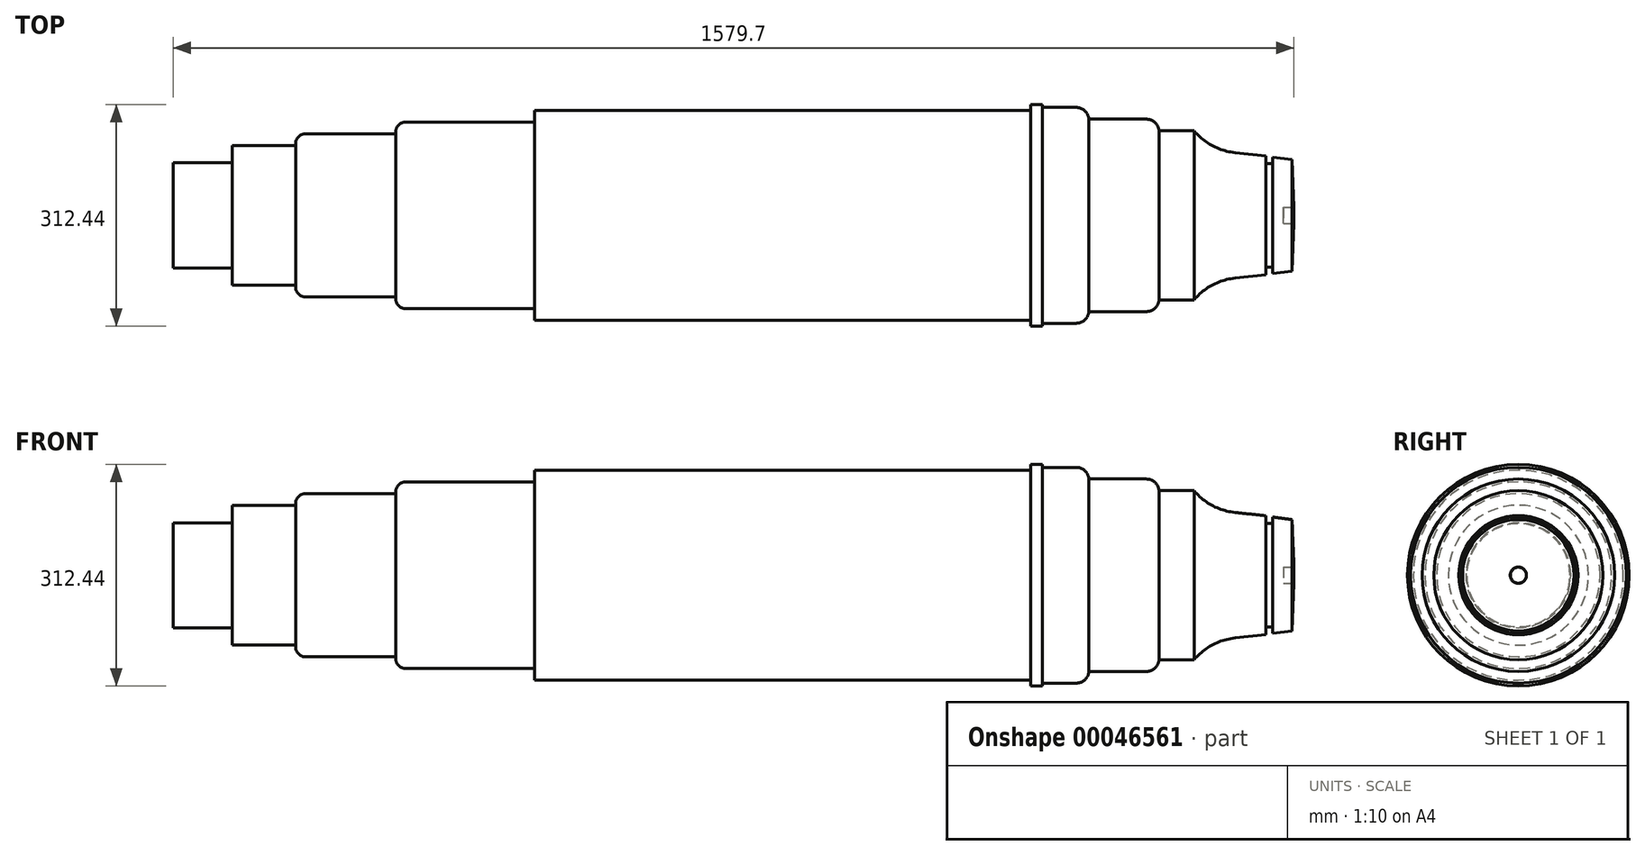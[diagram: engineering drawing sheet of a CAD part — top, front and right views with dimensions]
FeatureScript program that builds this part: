
annotation { "Feature Type Name" : "Feature", "Feature Type Description" : "" }
export const myFeature = defineFeature(function(context is Context, id is Id, definition is map)
    precondition{}
    {
        {
            var Q0;
            Q0=qCreatedBy(makeId("Front.planeOp"),FACE);
            var sketch = newSketch(context, id + "F0", { "sketchPlane" : qUnion([Q0])});
            skLineSegment(sketch, "E0", {"start": v(-826.12, 0) * mm, "end": v(-826.12, 74) * mm});
            skLineSegment(sketch, "E1", {"start": v(-826.12, 74) * mm, "end": v(-742.99, 74) * mm});
            skLineSegment(sketch, "E2", {"start": v(-742.99, 74) * mm, "end": v(-742.99, 98.67) * mm});
            skLineSegment(sketch, "E3", {"start": v(-742.99, 98.67) * mm, "end": v(-653.4, 98.67) * mm});
            skLineSegment(sketch, "E4", {"start": v(-653.4, 98.67) * mm, "end": v(-653.4, 115.11) * mm});
            skLineSegment(sketch, "E5", {"start": v(-653.4, 115.11) * mm, "end": v(-512.26, 115.11) * mm});
            skLineSegment(sketch, "E6", {"start": v(-512.26, 115.11) * mm, "end": v(-512.26, 131.56) * mm});
            skLineSegment(sketch, "E7", {"start": v(-512.26, 131.56) * mm, "end": v(-316.4, 131.56) * mm});
            skLineSegment(sketch, "E8", {"start": v(-316.4, 131.56) * mm, "end": v(-316.4, 148) * mm});
            skLineSegment(sketch, "E9", {"start": v(-316.4, 148) * mm, "end": v(382.5, 148) * mm});
            skLineSegment(sketch, "E10", {"start": v(382.5, 148) * mm, "end": v(382.5, 156.22) * mm});
            skLineSegment(sketch, "E11", {"start": v(382.5, 156.22) * mm, "end": v(398.94, 156.22) * mm});
            skLineSegment(sketch, "E12", {"start": v(398.94, 156.22) * mm, "end": v(398.94, 152.11) * mm});
            skLineSegment(sketch, "E13", {"start": v(398.94, 152.11) * mm, "end": v(464.71, 152.11) * mm});
            skLineSegment(sketch, "E14", {"start": v(464.71, 152.11) * mm, "end": v(464.71, 135.67) * mm});
            skLineSegment(sketch, "E15", {"start": v(464.71, 135.67) * mm, "end": v(563.38, 135.67) * mm});
            skLineSegment(sketch, "E16", {"start": v(563.38, 135.67) * mm, "end": v(563.38, 119.22) * mm});
            skLineSegment(sketch, "E17", {"start": v(563.38, 119.22) * mm, "end": v(612.71, 119.22) * mm});
            skLineSegment(sketch, "E18", {"start": v(612.71, 119.22) * mm, "end": v(612.71, 94.48) * mm});
            skLineSegment(sketch, "E19", {"start": v(-826.12, 0) * mm, "end": v(715.79, 0) * mm});
            skLineSegment(sketch, "E20", {"start": v(612.71, 94.48) * mm, "end": v(714.03, 84) * mm});
            skLineSegment(sketch, "E21", {"start": v(714.27, 72.73) * mm, "end": v(723.81, 72.93) * mm});
            skLineSegment(sketch, "E22", {"start": v(723.81, 72.93) * mm, "end": v(723.62, 82.1) * mm});
            skLineSegment(sketch, "E23", {"start": v(723.62, 82.1) * mm, "end": v(750.85, 78.46) * mm});
            skLineSegment(sketch, "E24", {"start": v(753.58, 11.5) * mm, "end": v(738.5, 11.24) * mm});
            skLineSegment(sketch, "E25", {"start": v(738.5, 11.24) * mm, "end": v(738.5, 0) * mm});
            skLineSegment(sketch, "E26", {"start": v(714.03, 84) * mm, "end": v(714.27, 72.73) * mm});
            skLineSegment(sketch, "E27", {"start": v(738.5, 0) * mm, "end": v(715.79, 0) * mm});
            skLineSegment(sketch, "E28", {"start": v(750.85, 78.46) * mm, "end": v(753.58, 11.5) * mm});
            skLineSegment(sketch, "E29", {"start": v(-907.22, 0) * mm, "end": v(1014.36, 0) * mm, "construction": true});
            skPoint(sketch, "E29.startSnap0", {"position": v(-55.17, 0) * mm});
            skPoint(sketch, "E29.endSnap0", {"position": v(-55.17, 0) * mm});
            skSolve(sketch);
        }
        {
            var Q0;
            Q0=qSketchRegion(id+"F0",true);
            var Q1;
            Q1=sQuery(id+"F0.wireOp",EDGE,"E29");
            revolve(context, id + "F1", {"entities" : qUnion([Q0]), "axis" : qUnion([Q1]), "revolveType" : RevolveType.FULL});
        }
        {
            var Q0;
            Q0=makeQuery(id+"F1.opRevolve","SWEPT_EDGE",EDGE,{"disambiguationData":[OSD([sQuery(id+"F0.wireOp",EDGE,"E4"),sQuery(id+"F0.wireOp",EDGE,"E5")])]});
            var Q1;
            Q1=makeQuery(id+"F1.opRevolve","SWEPT_EDGE",EDGE,{"disambiguationData":[OSD([sQuery(id+"F0.wireOp",EDGE,"E6"),sQuery(id+"F0.wireOp",EDGE,"E7")])]});
            fillet(context, id + "F2", {"entities" : qUnion([Q0, Q1]), "radius" : 14 * mm, "tangentPropagation" : true, "allowEdgeOverflow" : false});
        }
        {
            var Q0;
            Q0=makeQuery(id+"F1.opRevolve","SWEPT_EDGE",EDGE,{"disambiguationData":[OSD([sQuery(id+"F0.wireOp",EDGE,"E15"),sQuery(id+"F0.wireOp",EDGE,"E16")])]});
            var Q1;
            Q1=makeQuery(id+"F1.opRevolve","SWEPT_EDGE",EDGE,{"disambiguationData":[OSD([sQuery(id+"F0.wireOp",EDGE,"E13"),sQuery(id+"F0.wireOp",EDGE,"E14")])]});
            fillet(context, id + "F3", {"entities" : qUnion([Q0, Q1]), "radius" : 18 * mm, "tangentPropagation" : true, "allowEdgeOverflow" : false});
        }
        {
            var Q0;
            Q0=makeQuery(id+"F1.opRevolve","SWEPT_EDGE",EDGE,{"disambiguationData":[OSD([sQuery(id+"F0.wireOp",EDGE,"E18"),sQuery(id+"F0.wireOp",EDGE,"E20")])]});
            fillet(context, id + "F4", {"entities" : qUnion([Q0]), "radius" : 87.1 * mm, "tangentPropagation" : true, "allowEdgeOverflow" : false});
        }
    });
